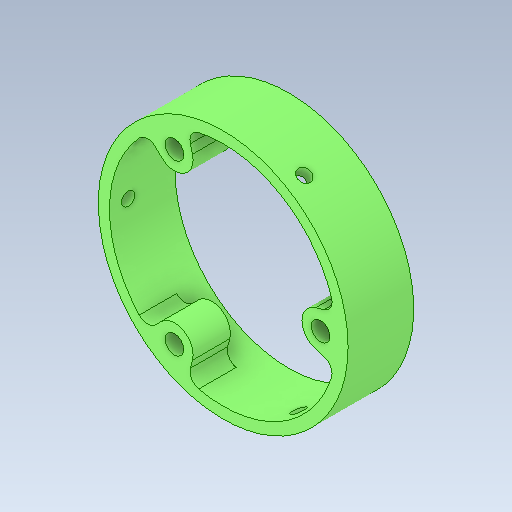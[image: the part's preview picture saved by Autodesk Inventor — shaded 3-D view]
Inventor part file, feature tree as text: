
AUTODESK INVENTOR PART (.ipt)
format: ipt  version: 2020 (Build 240168000, 168)  size: 221,696 bytes
history: native  units: in
note: dims shown in document units (in); Inventor stores cm internally (conversion verified against a paired STEP export)
features: sketch x5, extrude x4, fillet x1, hole x1, pattern_circular x1
ambient origin geometry x8: Origin, YZ Plane, XZ Plane, XY Plane, X Axis, Y Axis, Z Axis, Center Point
bodies: Solid1 (feature_tree)
feature tree (12):
  extrude  "Extrusion1"  Depth=1.675in
  extrude  "Extrusion2"  Depth=0.25in
  fillet  "Fillet1"  Radius=0.1374in
  hole  "Hole1"  [1 undecoded]
  extrude  "Extrusion7"  Depth=0.075in
  pattern_circular  "Circular Pattern1"  [2 undecoded]
  extrude  "Extrusion8"  Depth=0.125in
  sketch  "Sketch1"  dims[d0=1.525in d1=1.675in]
  sketch  "Sketch2"  dims[d2=0.25in d3=0.0in d5=0.25in d6=0.1374in]
  sketch  "Sketch3"  dims[d7=30.0deg d8=1.1811in d10=360.0deg]
  sketch  "Sketch11"  dims[d12=0.25in d13=0.0in d14=0.075in]
  sketch  "Sketch12"  dims[d15=0.125in d16=0.75in d17=0.375in d18=0.25in d19=0.5635in d20=1.0in d21=0.8108in d51=0.089in d52=0.125in d53=0.25in d54=1.0in d55=0.0in d56=1.1811in d57=360.0deg d59=0.5283in d60=0.19in d61=0.0in d62=1.5in d63=1.5in d65=0.98in]
note: 3 required parameter values undecoded (feature->parameter linkage not recoverable at this tier; creation-order binding heuristic only, values carry confidence <= 0.55)
